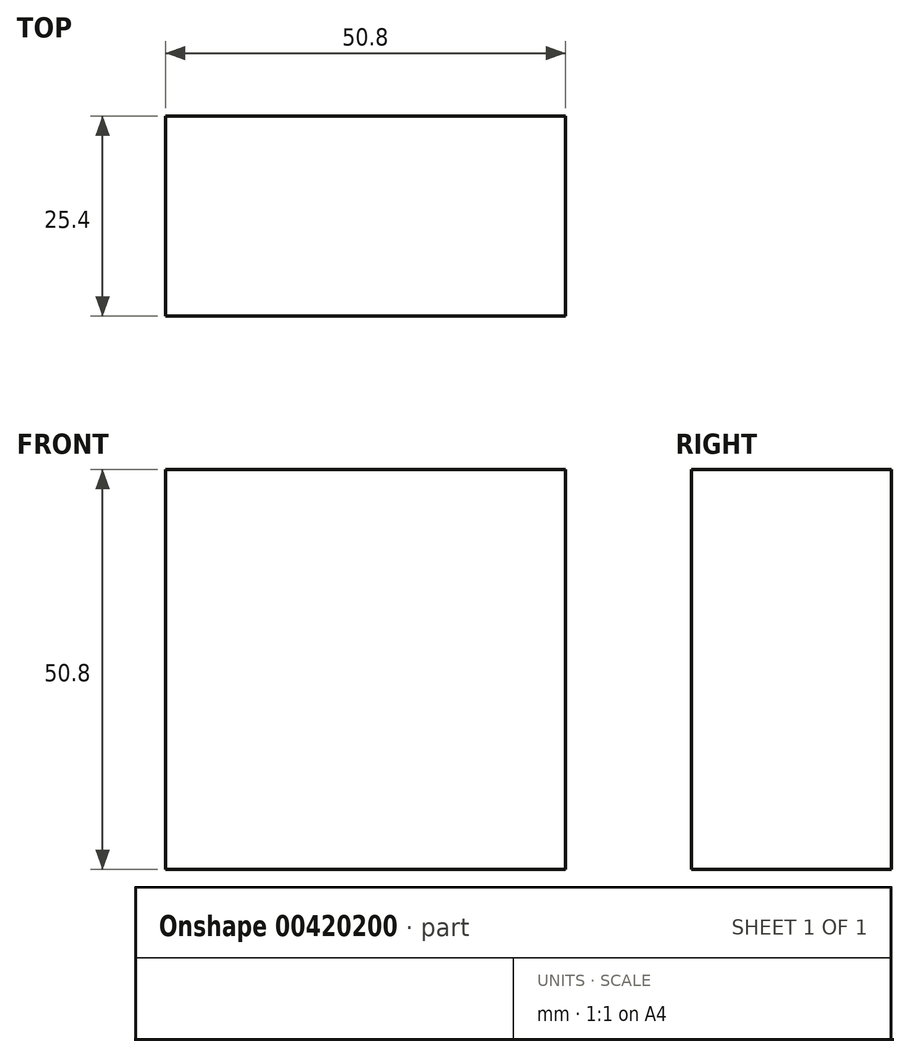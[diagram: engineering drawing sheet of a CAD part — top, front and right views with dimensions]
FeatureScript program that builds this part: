
annotation { "Feature Type Name" : "Feature", "Feature Type Description" : "" }
export const myFeature = defineFeature(function(context is Context, id is Id, definition is map)
    precondition{}
    {
        {
            var Q0;
            Q0=qCreatedBy(makeId("Front.planeOp"),FACE);
            var sketch = newSketch(context, id + "F0", { "sketchPlane" : qUnion([Q0])});
            skLineSegment(sketch, "E0", {"start": v(0, 0) * mm, "end": v(0, 50.8) * mm});
            skLineSegment(sketch, "E1", {"start": v(0, 50.8) * mm, "end": v(50.8, 50.8) * mm});
            skLineSegment(sketch, "E2", {"start": v(50.8, 50.8) * mm, "end": v(50.8, 0) * mm});
            skLineSegment(sketch, "E3", {"start": v(50.8, 0) * mm, "end": v(0, 0) * mm});
            skSolve(sketch);
        }
        {
            var Q0;
            Q0=makeQuery(id+"F0.imprint","IMPRINT",FACE,{"disambiguationData":[TD([[makeQuery(id+"F0.imprint","IMPRINT",EDGE,{"derivedFrom":sQuery(id+"F0.wireOp",EDGE,"E0")}),-1.0]])]});
            extrude(context, id + "F1", {"entities" : qUnion([Q0]), "depth" : 25.4 * mm});
        }
    });
